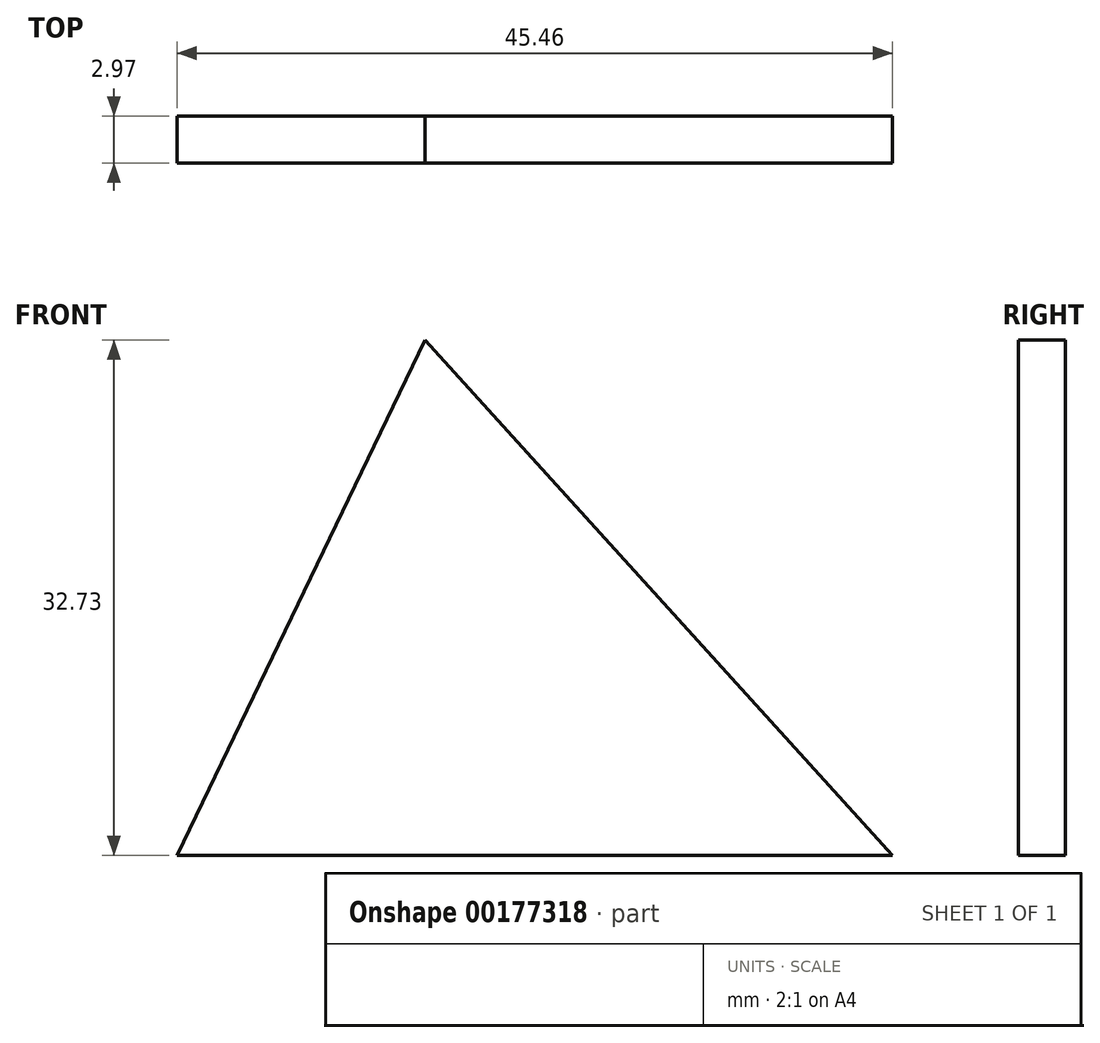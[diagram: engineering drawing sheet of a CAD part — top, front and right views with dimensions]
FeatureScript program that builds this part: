
annotation { "Feature Type Name" : "Feature", "Feature Type Description" : "" }
export const myFeature = defineFeature(function(context is Context, id is Id, definition is map)
    precondition{}
    {
        {
            var Q0;
            Q0=qCreatedBy(makeId("Front.planeOp"),FACE);
            var sketch = newSketch(context, id + "F0", { "sketchPlane" : qUnion([Q0])});
            skLineSegment(sketch, "E0", {"start": v(-12.43, 20.3) * mm, "end": v(-57.89, 20.3) * mm});
            skLineSegment(sketch, "E1", {"start": v(-12.43, 20.3) * mm, "end": v(-42.13, 53.04) * mm});
            skLineSegment(sketch, "E2", {"start": v(-42.13, 53.04) * mm, "end": v(-57.89, 20.3) * mm});
            skSolve(sketch);
        }
        {
            var Q0;
            Q0 = qSketchRegion(id + "F0", true);
            extrude(context, id + "F1", {"entities" : qUnion([Q0]), "depth" : 2.97 * mm});
        }
    });
